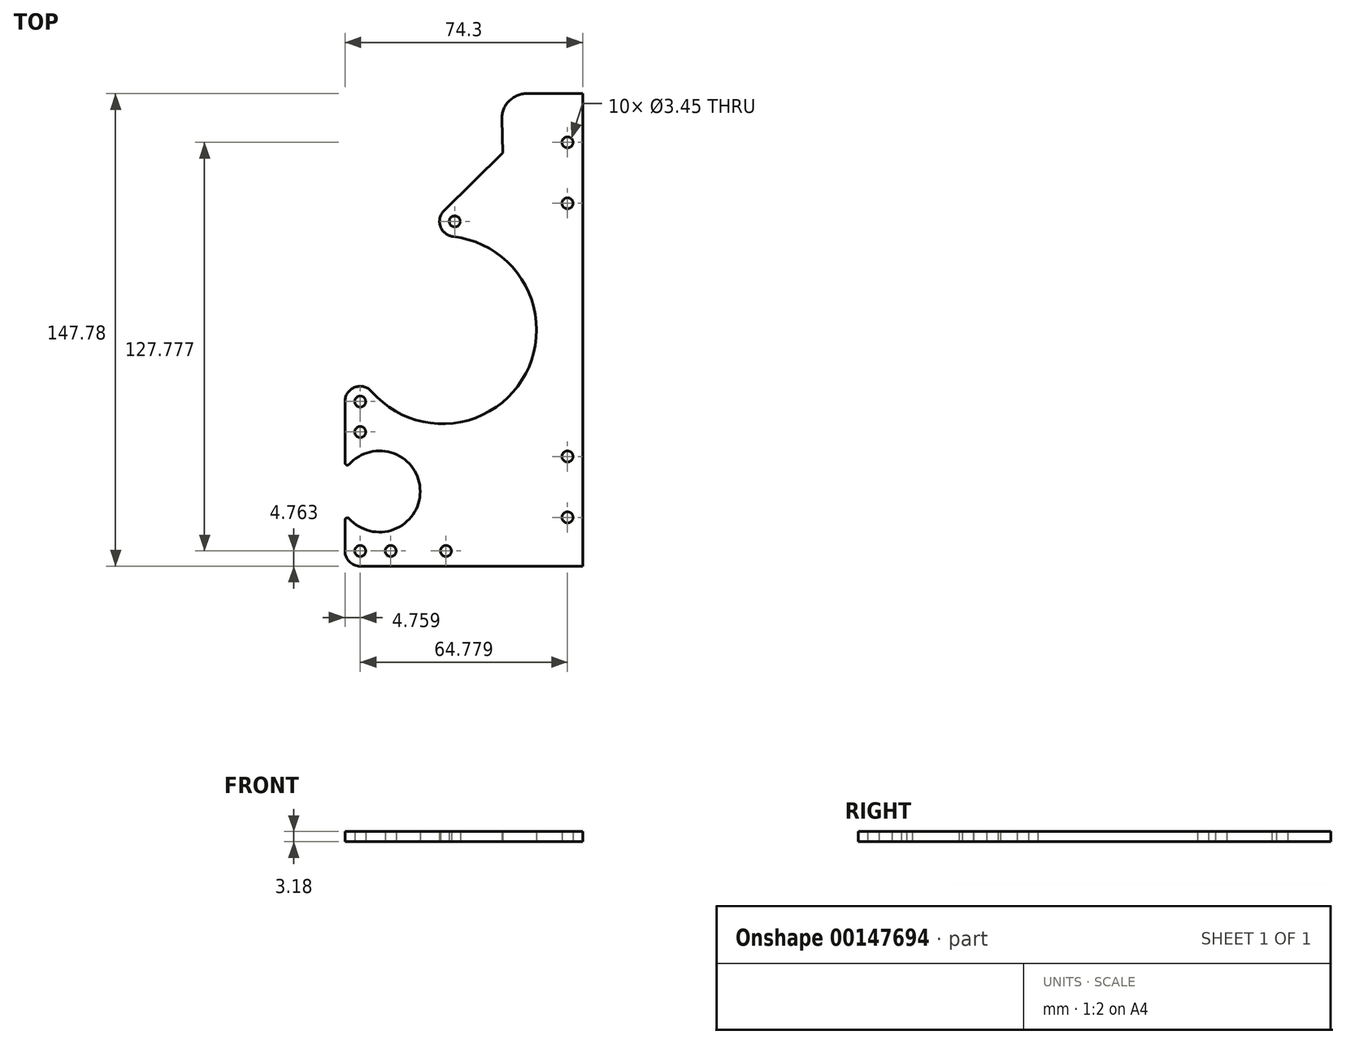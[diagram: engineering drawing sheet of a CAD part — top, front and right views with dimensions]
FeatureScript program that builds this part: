
annotation { "Feature Type Name" : "Feature", "Feature Type Description" : "" }
export const myFeature = defineFeature(function(context is Context, id is Id, definition is map)
    precondition{}
    {
        {
            var Q0;
            Q0=qCreatedBy(makeId("Top.planeOp"),FACE);
            var sketch = newSketch(context, id + "F0", { "sketchPlane" : qUnion([Q0])});
            skLineSegment(sketch, "E0.bottom", {"start": v(43.8, -73.89) * mm, "end": v(-25.75, -73.89) * mm});
            skLineSegment(sketch, "E0.top", {"start": v(43.8, 73.89) * mm, "end": v(26.32, 73.89) * mm});
            skLineSegment(sketch, "E0.left", {"start": v(43.8, -73.89) * mm, "end": v(43.8, 73.89) * mm});
            skLineSegment(sketch, "E1", {"start": v(39.03, -73.89) * mm, "end": v(39.03, -58.65) * mm, "construction": true});
            skLineSegment(sketch, "E2", {"start": v(39.03, -58.65) * mm, "end": v(39.03, -39.6) * mm, "construction": true});
            skLineSegment(sketch, "E3", {"start": v(39.03, 73.89) * mm, "end": v(39.03, 58.65) * mm, "construction": true});
            skLineSegment(sketch, "E4", {"start": v(39.03, 58.65) * mm, "end": v(39.03, 39.6) * mm, "construction": true});
            skCircle(sketch, "E5", {"center": v(39.03, 58.65) * mm, "radius": 1.73 * mm});
            skCircle(sketch, "E6", {"center": v(39.03, 39.6) * mm, "radius": 1.73 * mm});
            skCircle(sketch, "E7", {"center": v(39.03, -39.6) * mm, "radius": 1.73 * mm});
            skCircle(sketch, "E8", {"center": v(39.03, -58.65) * mm, "radius": 1.73 * mm});
            skArc(sketch, "E9", {"start": v(-30.51, -69.13) * mm, "mid": v(-29.12, -72.5) * mm, "end": v(-25.75, -73.89) * mm});
            skArc(sketch, "E10", {"start": v(-22.16, -19.28) * mm, "mid": v(26, -13.65) * mm, "end": v(3.28, 29.18) * mm});
            skArc(sketch, "E11", {"start": v(0.47, 37.3) * mm, "mid": v(-0.69, 32.36) * mm, "end": v(3.28, 29.18) * mm});
            skArc(sketch, "E12", {"start": v(-22.16, -19.28) * mm, "mid": v(-27.42, -17.94) * mm, "end": v(-30.51, -22.4) * mm});
            skCircle(sketch, "E13", {"center": v(-25.75, -22.4) * mm, "radius": 1.73 * mm});
            skCircle(sketch, "E14", {"center": v(3.81, 33.92) * mm, "radius": 1.73 * mm});
            skCircle(sketch, "E15", {"center": v(-25.75, -69.13) * mm, "radius": 1.73 * mm});
            skLineSegment(sketch, "E16", {"start": v(43.8, 0) * mm, "end": v(21.9, 0) * mm, "construction": true});
            skLineSegment(sketch, "E17", {"start": v(21.9, 0) * mm, "end": v(21.9, 0) * mm});
            skLineSegment(sketch, "E18", {"start": v(21.9, 0) * mm, "end": v(0, 0) * mm, "construction": true});
            skLineSegment(sketch, "E19", {"start": v(-25.75, -69.13) * mm, "end": v(-16.23, -69.13) * mm, "construction": true});
            skLineSegment(sketch, "E20", {"start": v(-16.23, -69.13) * mm, "end": v(1.05, -69.13) * mm, "construction": true});
            skCircle(sketch, "E21", {"center": v(1.05, -69.13) * mm, "radius": 1.73 * mm});
            skLineSegment(sketch, "E22", {"start": v(-25.75, -69.13) * mm, "end": v(-25.75, -31.93) * mm, "construction": true});
            skCircle(sketch, "E23", {"center": v(-25.75, -31.93) * mm, "radius": 1.73 * mm});
            skCircle(sketch, "E24", {"center": v(-16.23, -69.13) * mm, "radius": 1.73 * mm});
            skLineSegment(sketch, "E25", {"start": v(-25.75, -31.93) * mm, "end": v(-25.75, -22.4) * mm, "construction": true});
            skArc(sketch, "E26", {"start": v(26.32, 73.89) * mm, "mid": v(20.73, 71.53) * mm, "end": v(18.53, 65.87) * mm});
            skLineSegment(sketch, "E27", {"start": v(0.47, 37.3) * mm, "end": v(18.83, 55.42) * mm});
            skLineSegment(sketch, "E28", {"start": v(18.53, 65.87) * mm, "end": v(18.83, 55.42) * mm});
            skLineSegment(sketch, "E29", {"start": v(1.05, -69.13) * mm, "end": v(1.05, -50.53) * mm, "construction": true});
            skLineSegment(sketch, "E30", {"start": v(1.05, -50.53) * mm, "end": v(-19.72, -50.53) * mm, "construction": true});
            skLineSegment(sketch, "E31", {"start": v(-30.51, -22.4) * mm, "end": v(-30.51, -43.82) * mm});
            skLineSegment(sketch, "E32", {"start": v(-30.51, -69.13) * mm, "end": v(-30.51, -57.23) * mm});
            skArc(sketch, "E33", {"start": v(-30.51, -57.23) * mm, "mid": v(-7.01, -50.53) * mm, "end": v(-30.51, -43.82) * mm});
            skSolve(sketch);
        }
        {
            var Q0;
            Q0=qSketchRegion(id+"F0",true);
            extrude(context, id + "F1", {"entities" : qUnion([Q0]), "depth" : 3.17 * mm});
        }
        {
            var Q0;
            Q0=makeQuery(id+"F1.opExtrude","SWEPT_EDGE",EDGE,{"disambiguationData":[OSD([sQuery(id+"F0.wireOp",EDGE,"E31"),sQuery(id+"F0.wireOp",EDGE,"E33")])]});
            var Q1;
            Q1=makeQuery(id+"F1.opExtrude","SWEPT_EDGE",EDGE,{"disambiguationData":[OSD([sQuery(id+"F0.wireOp",EDGE,"E32"),sQuery(id+"F0.wireOp",EDGE,"E33")])]});
            fillet(context, id + "F2", {"entities" : qUnion([Q0, Q1]), "radius" : 0.76 * mm, "tangentPropagation" : true, "allowEdgeOverflow" : false});
        }
    });
